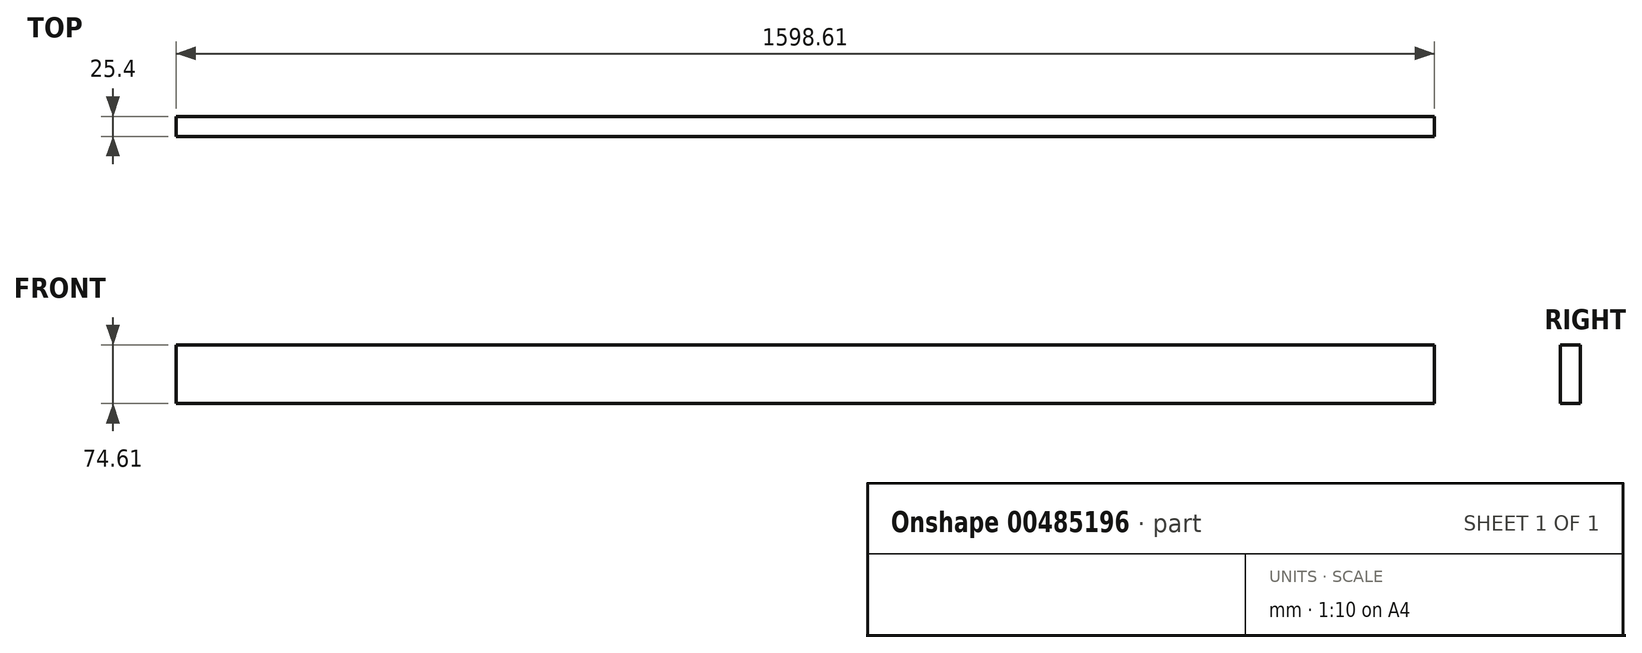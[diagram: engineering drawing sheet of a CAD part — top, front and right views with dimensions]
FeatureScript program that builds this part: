
annotation { "Feature Type Name" : "Feature", "Feature Type Description" : "" }
export const myFeature = defineFeature(function(context is Context, id is Id, definition is map)
    precondition{}
    {
        {
            var Q0;
            Q0=qCreatedBy(makeId("Front.planeOp"),FACE);
            var sketch = newSketch(context, id + "F0", { "sketchPlane" : qUnion([Q0])});
            skLineSegment(sketch, "E0.bottom", {"start": v(0, 0) * mm, "end": v(1598.61, 0) * mm});
            skLineSegment(sketch, "E0.top", {"start": v(0, -74.61) * mm, "end": v(1598.61, -74.61) * mm});
            skLineSegment(sketch, "E0.left", {"start": v(0, 0) * mm, "end": v(0, -74.61) * mm});
            skLineSegment(sketch, "E0.right", {"start": v(1598.61, 0) * mm, "end": v(1598.61, -74.61) * mm});
            skSolve(sketch);
        }
        {
            var Q0;
            Q0 = qSketchRegion(id + "F0", true);
            extrude(context, id + "F1", {"entities" : qUnion([Q0]), "oppositeDirection" : true, "depth" : 25.4 * mm});
        }
    });
